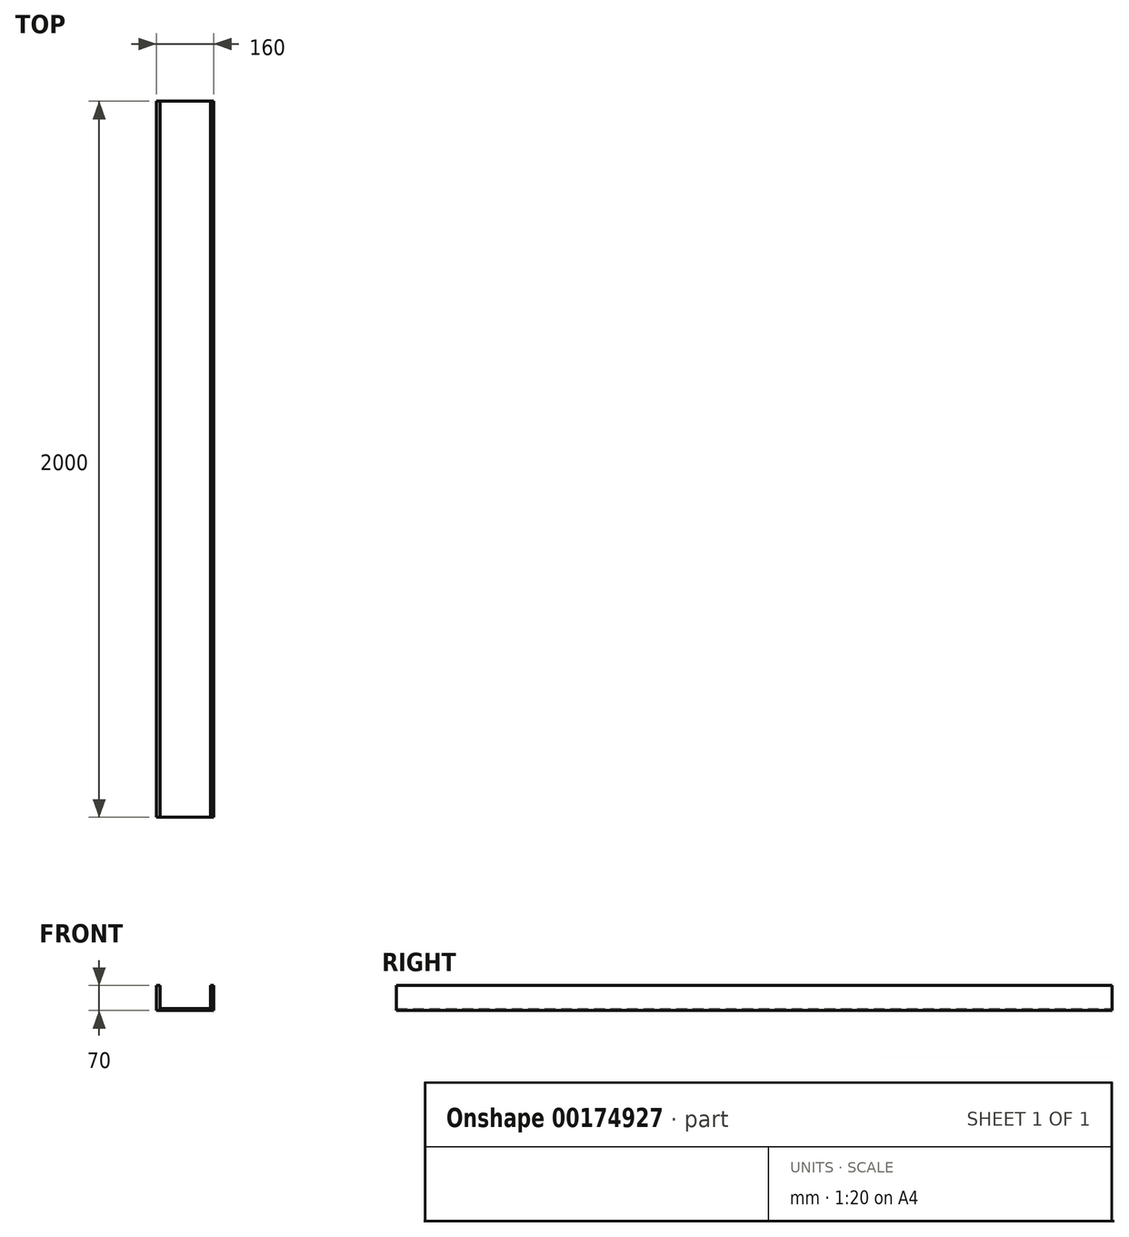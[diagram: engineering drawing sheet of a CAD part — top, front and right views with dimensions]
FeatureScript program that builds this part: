
annotation { "Feature Type Name" : "Feature", "Feature Type Description" : "" }
export const myFeature = defineFeature(function(context is Context, id is Id, definition is map)
    precondition{}
    {
        {
            var Q0;
            Q0=qCreatedBy(makeId("Front.planeOp"),FACE);
            var sketch = newSketch(context, id + "F0", { "sketchPlane" : qUnion([Q0])});
            skLineSegment(sketch, "E0", {"start": v(0, 0) * mm, "end": v(160, 0) * mm});
            skLineSegment(sketch, "E1", {"start": v(160, 0) * mm, "end": v(160, 70) * mm});
            skLineSegment(sketch, "E2", {"start": v(160, 70) * mm, "end": v(150.5, 70) * mm});
            skLineSegment(sketch, "E3", {"start": v(150.5, 70) * mm, "end": v(150.5, 5.5) * mm});
            skLineSegment(sketch, "E4", {"start": v(150.5, 5.5) * mm, "end": v(9.5, 5.5) * mm});
            skLineSegment(sketch, "E5", {"start": v(9.5, 5.5) * mm, "end": v(9.5, 70) * mm});
            skLineSegment(sketch, "E6", {"start": v(9.5, 70) * mm, "end": v(0, 70) * mm});
            skLineSegment(sketch, "E7", {"start": v(0, 70) * mm, "end": v(0, 0) * mm});
            skSolve(sketch);
        }
        {
            var Q0;
            Q0=qSketchRegion(id+"F0",true);
            extrude(context, id + "F1", {"entities" : qUnion([Q0]), "depth" : 2000 * mm});
        }
    });
